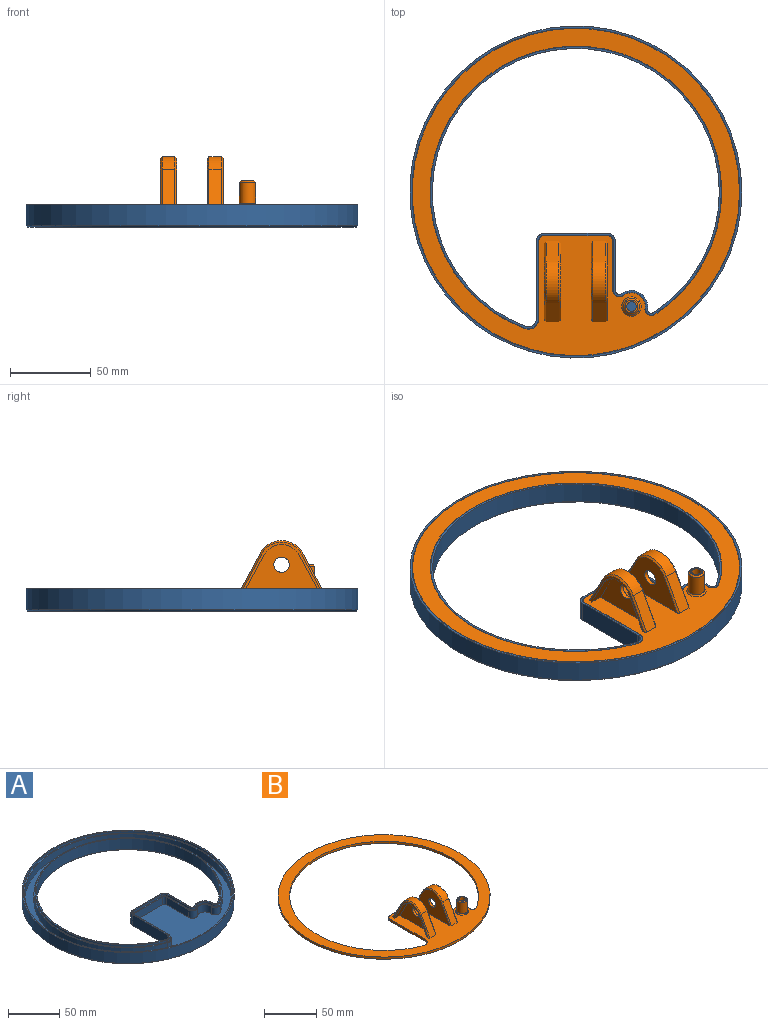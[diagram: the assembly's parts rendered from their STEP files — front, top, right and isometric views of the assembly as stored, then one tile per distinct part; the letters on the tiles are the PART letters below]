
ASSEMBLY  parts=2 mates=1
PART A: 50 faces, bbox 206x206x14 mm
  f0: plane 180.5x175.15mm, normal (0,0,1), area 822.3mm2, adj f1,f2,f3,f4,f5,f6,f7,f8
  f1: cylinder r=2.5mm len=13mm, axis (0,0,-1), area 72mm2, adj f0,f2,f11,f40
  f2: plane 30.51x13mm, normal (1,0,0), area 396.6mm2, adj f0,f1,f3,f39
  f3: cylinder r=5mm len=13mm, axis (0,0,-1), area 102.1mm2, adj f0,f2,f4,f41
  f4: plane 39x13mm, normal (0,1,0), area 507mm2, adj f0,f3,f5,f43
  f5: cylinder r=5mm len=13mm, axis (0,0,-1), area 102.1mm2, adj f0,f4,f6,f45
  f6: plane 48.09x13mm, normal (-1,0,0), area 625.1mm2, adj f0,f5,f7,f47
  f7: cylinder r=5mm len=13mm, axis (0,0,-1), area 125.4mm2, adj f0,f6,f8,f48
  f8: cylinder r=89mm len=178mm, axis (0,0,-1), area 6191.5mm2, adj f0,f7,f9,f46
  f9: cylinder r=2.5mm len=13mm, axis (0,0,-1), area 73.9mm2, adj f0,f8,f11,f44
  f10: cylinder r=103mm len=206mm, axis (0,0,-1), area 8413.2mm2, adj f12,f49
  f11: cylinder r=10mm len=16mm, axis (0,0,-1), area 304.7mm2, adj f0,f1,f9,f42
  f12: plane 206x206mm, normal (0,0,1), area 804.1mm2, adj f10,f25
  f13: plane 204x204mm, normal (0,0,-1), area 10581.9mm2, adj f39,f40,f41,f42,f43,f44,f45,f46
  f14: plane 183x177.65mm, normal (0,0,1), area 832.1mm2, adj f15,f16,f17,f18,f19,f20,f21,f22
  f15: cylinder r=6.25mm len=8.45mm, axis (0,0,1), area 30.2mm2, adj f0,f14,f16,f24
  f16: plane 48.09x2.5mm, normal (1,0,0), area 120.2mm2, adj f0,f14,f15,f17
  f17: cylinder r=3.75mm len=3.75mm, axis (0,0,1), area 14.7mm2, adj f0,f14,f16,f18
  f18: plane 39x2.5mm, normal (0,-1,0), area 97.5mm2, adj f0,f14,f17,f19
  f19: cylinder r=3.75mm len=3.75mm, axis (0,0,1), area 14.7mm2, adj f0,f14,f18,f20
  f20: plane 30.51x2.5mm, normal (-1,0,0), area 76.3mm2, adj f0,f14,f19,f21
  f21: cylinder r=3.75mm len=6mm, axis (0,0,1), area 20.8mm2, adj f0,f14,f20,f22
  f22: cylinder r=8.75mm len=14mm, axis (0,0,1), area 51.3mm2, adj f0,f14,f21,f23
  f23: cylinder r=3.75mm len=5.78mm, axis (0,0,1), area 21.3mm2, adj f0,f14,f22,f24
  f24: cylinder r=90.25mm len=180.5mm, axis (0,0,1), area 1207.4mm2, adj f0,f14,f15,f23
  f25: cylinder r=101.75mm len=203.5mm, axis (0,0,1), area 1598.3mm2, adj f12,f26
  f26: plane 203.5x203.5mm, normal (0,0,1), area 794.2mm2, adj f25,f27
  f27: cylinder r=100.5mm len=201mm, axis (0,0,-1), area 5683.1mm2, adj f26,f28
  f28: plane 201x201mm, normal (0,0,1), area 8630.3mm2, adj f27,f29,f30,f31,f32,f33,f34,f35
  f29: cylinder r=7.5mm len=12mm, axis (0,0,-1), area 158.2mm2, adj f14,f28,f30,f38
  f30: cylinder r=5mm len=9mm, axis (0,0,-1), area 102.3mm2, adj f14,f28,f29,f31
  f31: cylinder r=91.5mm len=183mm, axis (0,0,-1), area 4406.8mm2, adj f14,f28,f30,f32
  f32: cylinder r=7.5mm len=10.13mm, axis (0,0,-1), area 130.3mm2, adj f14,f28,f31,f33
  f33: plane 48.09x9mm, normal (1,0,0), area 432.8mm2, adj f14,f28,f32,f34
  f34: cylinder r=2.5mm len=9mm, axis (0,0,-1), area 35.3mm2, adj f14,f28,f33,f35
  f35: plane 39x9mm, normal (0,-1,0), area 351mm2, adj f14,f28,f34,f36
  f36: cylinder r=2.5mm len=9mm, axis (0,0,-1), area 35.3mm2, adj f14,f28,f35,f37
  f37: plane 30.51x9mm, normal (-1,0,0), area 274.6mm2, adj f14,f28,f36,f38
  f38: cylinder r=5mm len=9mm, axis (0,0,-1), area 99.6mm2, adj f14,f28,f29,f37
  f39: plane 30.51x1mm, normal (0.71,0,-0.71), area 43.1mm2, adj f2,f13,f40,f41
  f40: cone r=3.5mm half-angle=45deg, axis (0,0,-1), area 9.4mm2, adj f1,f13,f39,f42
  f41: cone r=5mm half-angle=45deg, axis (0,0,1), area 10mm2, adj f3,f13,f39,f43
  f42: cone r=10mm half-angle=45deg, axis (0,0,1), area 31.5mm2, adj f11,f13,f40,f44
  f43: plane 39x1mm, normal (0,0.71,-0.71), area 55.2mm2, adj f4,f13,f41,f45
  f44: cone r=3.5mm half-angle=45deg, axis (0,0,-1), area 9.6mm2, adj f9,f13,f42,f46
  f45: cone r=5mm half-angle=45deg, axis (0,0,1), area 10mm2, adj f5,f13,f43,f47
  f46: cone r=90mm half-angle=45deg, axis (0,0,-1), area 677.3mm2, adj f8,f13,f44,f48
  f47: plane 48.09x1mm, normal (-0.71,0,-0.71), area 68mm2, adj f6,f13,f45,f48
  f48: cone r=6mm half-angle=45deg, axis (0,0,-1), area 15mm2, adj f7,f13,f46,f47
  f49: cone r=103mm half-angle=45deg, axis (0,0,1), area 910.8mm2, adj f10,f13
PART B: 50 faces, bbox 203x203x32.5 mm
  f0: plane 47.73x29mm, normal (-1,0,0), area 115.2mm2, adj f4,f31,f32,f33,f42,f43,f44
  f1: cylinder r=4.75mm len=9.5mm, axis (-1,0,0), area 74.6mm2, adj f2,f34
  f2: plane 47.73x29mm, normal (1,0,0), area 841.5mm2, adj f1,f4,f36,f37,f38
  f3: plane 47.73x29mm, normal (-1,0,0), area 841.5mm2, adj f4,f24,f39,f40,f41
  f4: plane 203x203mm, normal (0,0,1), area 9487.8mm2, adj f0,f2,f3,f5,f6,f7,f8,f9
  f5: cylinder r=90.5mm len=181mm, axis (0,0,-1), area 1210.7mm2, adj f4,f6,f14,f16
  f6: cylinder r=4mm len=6.17mm, axis (0,0,-1), area 22.7mm2, adj f4,f5,f7,f16
  f7: cylinder r=8.5mm len=13.6mm, axis (0,0,-1), area 49.8mm2, adj f4,f6,f8,f16
  f8: cylinder r=4mm len=6.4mm, axis (0,0,-1), area 22.1mm2, adj f4,f7,f9,f16
  f9: plane 30.51x2.5mm, normal (1,0,0), area 76.3mm2, adj f4,f8,f10,f16
  f10: cylinder r=3.5mm len=3.5mm, axis (0,0,-1), area 13.7mm2, adj f4,f9,f11,f16
  f11: plane 39x2.5mm, normal (0,1,0), area 97.5mm2, adj f4,f10,f12,f16
  f12: cylinder r=3.5mm len=3.5mm, axis (0,0,-1), area 13.7mm2, adj f4,f11,f13,f16
  f13: plane 48.09x2.5mm, normal (-1,0,0), area 120.2mm2, adj f4,f12,f14,f16
  f14: cylinder r=6.5mm len=8.78mm, axis (0,0,-1), area 31.4mm2, adj f4,f5,f13,f16
  f15: cylinder r=101.5mm len=203mm, axis (0,0,-1), area 1594.4mm2, adj f4,f16
  f16: plane 203x203mm, normal (0,0,-1), area 9903.1mm2, adj f5,f6,f7,f8,f9,f10,f11,f12
  f17: plane 47.73x29mm, normal (1,0,0), area 115.2mm2, adj f4,f28,f29,f30,f45,f46,f47
  f18: cylinder r=5mm len=13mm, axis (0,0,-1), area 408.4mm2, adj f48,f49
  f19: plane 8x8mm, normal (0,0,1), area 22mm2, adj f35,f49
  f20: cylinder r=15mm len=26.47mm, axis (-1,0,0), area 259.4mm2, adj f21,f25,f40,f46
  f21: plane 22.06x11.76mm, normal (0,-0.88,0.47), area 200mm2, adj f4,f20,f39,f45
  f22: plane 22.06x11.76mm, normal (0,-0.88,0.47), area 200mm2, adj f4,f23,f36,f44
  f23: cylinder r=15mm len=26.47mm, axis (-1,0,0), area 259.4mm2, adj f22,f26,f37,f43
  f24: cylinder r=4.75mm len=9.5mm, axis (-1,0,0), area 74.6mm2, adj f3,f27
  f25: plane 22.06x11.76mm, normal (0,0.88,0.47), area 200mm2, adj f4,f20,f41,f47
  f26: plane 22.06x11.76mm, normal (0,0.88,0.47), area 200mm2, adj f4,f23,f38,f42
  f27: plane 44.33x27.5mm, normal (1,0,0), area 726.3mm2, adj f4,f24,f28,f29,f30
  f28: cylinder r=12.5mm len=22.06mm, axis (-1,0,0), area 202.7mm2, adj f17,f27,f29,f30
  f29: plane 20.88x11.14mm, normal (0,0.88,-0.47), area 177.5mm2, adj f4,f17,f27,f28
  f30: plane 20.88x11.14mm, normal (0,-0.88,-0.47), area 177.5mm2, adj f4,f17,f27,f28
  f31: plane 20.88x11.14mm, normal (0,-0.88,-0.47), area 177.5mm2, adj f0,f4,f32,f34
  f32: cylinder r=12.5mm len=22.06mm, axis (-1,0,0), area 202.7mm2, adj f0,f31,f33,f34
  f33: plane 20.88x11.14mm, normal (0,0.88,-0.47), area 177.5mm2, adj f0,f4,f32,f34
  f34: plane 44.33x27.5mm, normal (-1,0,0), area 726.3mm2, adj f1,f4,f31,f32,f33
  f35: cylinder r=3mm len=17.5mm, axis (0,0,1), area 329.9mm2, adj f16,f19
  f36: plane 22.06x12.65mm, normal (0.71,-0.62,0.33), area 35mm2, adj f2,f4,f22,f37
  f37: cone r=14mm half-angle=45deg, axis (-1,0,0), area 44.3mm2, adj f2,f23,f36,f38
  f38: plane 22.06x12.65mm, normal (0.71,0.62,0.33), area 35mm2, adj f2,f4,f26,f37
  f39: plane 22.06x12.65mm, normal (-0.71,-0.62,0.33), area 35mm2, adj f3,f4,f21,f40
  f40: cone r=15mm half-angle=45deg, axis (1,0,0), area 44.3mm2, adj f3,f20,f39,f41
  f41: plane 22.06x12.65mm, normal (-0.71,0.62,0.33), area 35mm2, adj f3,f4,f25,f40
  f42: plane 22.06x12.65mm, normal (-0.71,0.62,0.33), area 35mm2, adj f0,f4,f26,f43
  f43: cone r=14mm half-angle=45deg, axis (1,0,0), area 44.3mm2, adj f0,f23,f42,f44
  f44: plane 22.06x12.65mm, normal (-0.71,-0.62,0.33), area 35mm2, adj f0,f4,f22,f43
  f45: plane 22.06x12.65mm, normal (0.71,-0.62,0.33), area 35mm2, adj f4,f17,f21,f46
  f46: cone r=14mm half-angle=45deg, axis (-1,0,0), area 44.3mm2, adj f17,f20,f45,f47
  f47: plane 22.06x12.65mm, normal (0.71,0.62,0.33), area 35mm2, adj f4,f17,f25,f46
  f48: cone r=5mm half-angle=45deg, axis (0,0,-1), area 48.9mm2, adj f4,f18
  f49: cone r=4mm half-angle=45deg, axis (0,0,-1), area 40mm2, adj f18,f19
PLACE A t=(0,0,86)mm
PLACE B t=(0,0,-2.5)mm
MATE fastened A.f5 <-> B.f12  axis (0,0,1) through (-19.5,-30.56,97.5)mm
